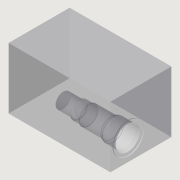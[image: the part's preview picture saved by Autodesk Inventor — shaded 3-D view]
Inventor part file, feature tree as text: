
AUTODESK INVENTOR PART (.ipt)
format: ipt  version: 2014 (Build 180170000, 170)  size: 214,016 bytes
history: native  units: mm
features: other x49, extrude x22, sketch x22
ambient origin geometry x8: Origin, YZ Plane, XZ Plane, XY Plane, X Axis, Y Axis, Z Axis, Center Point
bodies: 实体1 (feature_tree), 实体2 (feature_tree)
feature tree (93):
  extrude  "拉伸1"  Depth=30.2mm
  other  "UCS1"
  other  "UCS2"
  other  "UCS3"
  other  "UCS4"
  other  "UCS5"
  other  "UCS6"
  extrude  "拉伸2"  Depth=18.0mm
  extrude  "拉伸3"  Depth=0.79mm
  extrude  "拉伸5"  Depth=22.22mm
  extrude  "拉伸6"  Depth=14.28mm
  extrude  "拉伸7"  Depth=16.5mm TaperAngle=0.0deg
  extrude  "拉伸8"  Depth=38.5mm TaperAngle=0.0deg
  extrude  "拉伸9"  Depth=12.0mm
  extrude  "拉伸10"  Depth=47.63mm
  extrude  "拉伸11"  Depth=63.5mm TaperAngle=0.0deg
  extrude  "拉伸12"  Depth=63.5mm
  extrude  "拉伸13"  Depth=140.0mm
  extrude  "拉伸14"  Depth=0.79mm
  extrude  "拉伸15"  Depth=2.74mm
  extrude  "拉伸16"  Depth=12.7mm TaperAngle=0.0deg
  extrude  "拉伸17"  Depth=60.0mm TaperAngle=0.0deg
  extrude  "拉伸18"  Depth=60.0mm
  extrude  "拉伸19"  Depth=60.0mm
  extrude  "拉伸20"  Depth=60.0mm TaperAngle=0.0deg
  extrude  "拉伸21"  Depth=60.0mm
  extrude  "拉伸22"  Depth=60.0mm
  extrude  "拉伸23"  Depth=60.0mm TaperAngle=0.0deg
  other  "删除面2"
  sketch  "草图1"  dims[d0=60.0mm d1=0.0mm]
  sketch  "草图2"  dims[d2=0.0mm d3=0.0mm d4=0.0mm d5=0.0mm d6=0.0mm d7=0.0mm]
  sketch  "草图3"  dims[d8=0.0mm d9=0.0mm d10=0.0mm d11=0.0mm d12=0.0mm d13=0.0mm]
  sketch  "草图6"  dims[d14=0.0mm d15=0.0mm d16=0.0mm d17=0.0mm d18=0.0mm d19=0.0mm]
  sketch  "草图7"  dims[d20=0.0mm d21=0.0mm d22=0.0mm d23=0.0mm d24=0.0mm d25=0.0mm]
  sketch  "草图8"  dims[d26=0.0mm d27=0.0mm d28=0.0mm d29=0.0mm d30=0.0mm d31=0.0mm]
  sketch  "草图9"  dims[d32=0.0mm d33=0.0mm d34=0.0mm d35=0.0mm d36=0.0mm d37=0.0mm d38=30.2mm]
  sketch  "草图10"  dims[d39=20.0mm d40=18.0mm]
  sketch  "草图11"  dims[d41=0.79mm d42=0.0mm d43=24.0mm]
  sketch  "草图12"  dims[d44=2.74mm d45=-2.617994mm d49=22.22mm]
  sketch  "草图13"  dims[d50=14.28mm d51=0.0mm d52=14.28mm d53=-7.853982mm]
  sketch  "草图14"  dims[d54=20.63mm d55=16.5mm d56=0.0mm]
  sketch  "草图16"  dims[d57=19.08mm d58=38.5mm d59=0.0mm]
  sketch  "草图17"  dims[d60=12.0mm d61=-5.235988mm d62=17.5mm]
  sketch  "草图18"  dims[d63=47.63mm d64=0.0mm d65=47.63mm d66=-10.471976mm]
  sketch  "草图19"  dims[d67=15.0mm d68=63.5mm d69=0.0mm]
  sketch  "草图20"  dims[d70=63.5mm d71=-10.297443mm d75=30.2mm]
  sketch  "草图21"  dims[d76=80.0mm d77=140.0mm]
  sketch  "草图22"  dims[d78=0.79mm d79=0.0mm d80=20.7mm]
  sketch  "草图23"  dims[d81=2.74mm d82=-2.617994mm d83=2.74mm d84=-7.853982mm]
  sketch  "草图24"  dims[d85=19.05mm d86=12.7mm d87=0.0mm]
  sketch  "草图25"  dims[d88=17.48mm d89=19.05mm d90=0.0mm d91=19.05mm d92=-10.471976mm d93=12.7mm d94=29.3mm d95=0.0mm d96=29.3mm d97=-10.471976mm d98=11.0mm d99=38.1mm d100=0.0mm d101=38.1mm d102=-10.297443mm d106=100.0mm d107=60.0mm]
  other  "UCS1: YZ 平面"
  other  "UCS1: XZ 平面"
  other  "UCS1: XY 平面"
  other  "UCS1: X 轴"
  other  "UCS1: Y 轴"
  other  "UCS1: Z 轴"
  other  "UCS1: 原点"
  other  "UCS2: YZ 平面"
  other  "UCS2: XZ 平面"
  other  "UCS2: XY 平面"
  other  "UCS2: X 轴"
  other  "UCS2: Y 轴"
  other  "UCS2: Z 轴"
  other  "UCS2: 原点"
  other  "UCS3: YZ 平面"
  other  "UCS3: XZ 平面"
  other  "UCS3: XY 平面"
  other  "UCS3: X 轴"
  other  "UCS3: Y 轴"
  other  "UCS3: Z 轴"
  other  "UCS3: 原点"
  other  "UCS4: YZ 平面"
  other  "UCS4: XZ 平面"
  other  "UCS4: XY 平面"
  other  "UCS4: X 轴"
  other  "UCS4: Y 轴"
  other  "UCS4: Z 轴"
  other  "UCS4: 原点"
  other  "UCS5: YZ 平面"
  other  "UCS5: XZ 平面"
  other  "UCS5: XY 平面"
  other  "UCS5: X 轴"
  other  "UCS5: Y 轴"
  other  "UCS5: Z 轴"
  other  "UCS5: 原点"
  other  "UCS6: YZ 平面"
  other  "UCS6: XZ 平面"
  other  "UCS6: XY 平面"
  other  "UCS6: X 轴"
  other  "UCS6: Y 轴"
  other  "UCS6: Z 轴"
  other  "UCS6: 原点"
